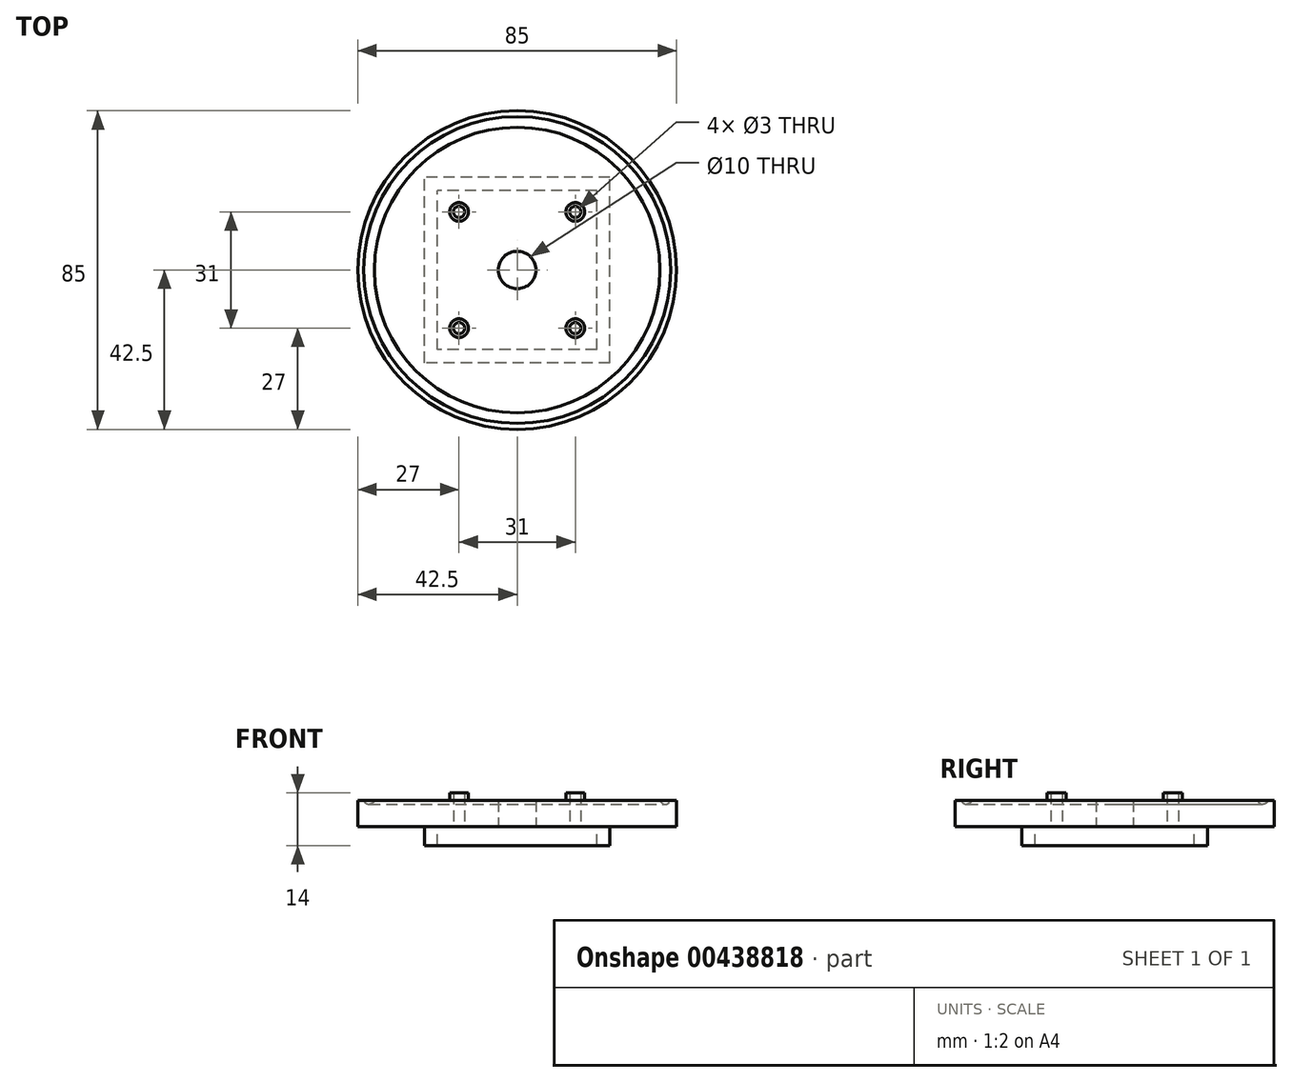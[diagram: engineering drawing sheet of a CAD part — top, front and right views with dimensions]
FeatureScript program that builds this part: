
annotation { "Feature Type Name" : "Feature", "Feature Type Description" : "" }
export const myFeature = defineFeature(function(context is Context, id is Id, definition is map)
    precondition{}
    {
        {
            var Q0;
            Q0=qCreatedBy(makeId("Top.planeOp"),FACE);
            var sketch = newSketch(context, id + "F0", { "sketchPlane" : qUnion([Q0])});
            skCircle(sketch, "E0", {"center": v(0, 0) * mm, "radius": 42.5 * mm});
            skLineSegment(sketch, "E1.bottom", {"start": v(21.25, 21.25) * mm, "end": v(-21.25, 21.25) * mm, "construction": true});
            skLineSegment(sketch, "E1.top", {"start": v(21.25, -21.25) * mm, "end": v(-21.25, -21.25) * mm, "construction": true});
            skLineSegment(sketch, "E1.left", {"start": v(21.25, 21.25) * mm, "end": v(21.25, -21.25) * mm, "construction": true});
            skLineSegment(sketch, "E1.right", {"start": v(-21.25, 21.25) * mm, "end": v(-21.25, -21.25) * mm, "construction": true});
            skLineSegment(sketch, "E2.bottom", {"start": v(15.5, 15.5) * mm, "end": v(-15.5, 15.5) * mm, "construction": true});
            skLineSegment(sketch, "E2.top", {"start": v(15.5, -15.5) * mm, "end": v(-15.5, -15.5) * mm, "construction": true});
            skLineSegment(sketch, "E2.left", {"start": v(15.5, 15.5) * mm, "end": v(15.5, -15.5) * mm, "construction": true});
            skLineSegment(sketch, "E2.right", {"start": v(-15.5, 15.5) * mm, "end": v(-15.5, -15.5) * mm, "construction": true});
            skCircle(sketch, "E3", {"center": v(-15.5, 15.5) * mm, "radius": 1.5 * mm});
            skCircle(sketch, "E4", {"center": v(15.5, 15.5) * mm, "radius": 1.5 * mm});
            skCircle(sketch, "E5", {"center": v(15.5, -15.5) * mm, "radius": 1.5 * mm});
            skCircle(sketch, "E6", {"center": v(-15.5, -15.5) * mm, "radius": 1.5 * mm});
            skCircle(sketch, "E7", {"center": v(0, 0) * mm, "radius": 5 * mm});
            skSolve(sketch);
        }
        {
            var Q0;
            Q0=makeQuery(id+"F0.imprint","IMPRINT",FACE,{"disambiguationData":[TD([[makeQuery(id+"F0.imprint","IMPRINT",EDGE,{"derivedFrom":sQuery(id+"F0.wireOp",EDGE,"E0")}),1.0]])]});
            extrude(context, id + "F1", {"entities" : qUnion([Q0]), "depth" : 7 * mm});
        }
        {
            var Q0;
            Q0=makeQuery(id+"F1.opExtrude","CAP_FACE",FACE,{"disambiguationData":[OSD([sQuery(id+"F0.wireOp",EDGE,"E0"),sQuery(id+"F0.wireOp",EDGE,"E3"),sQuery(id+"F0.wireOp",EDGE,"E4"),sQuery(id+"F0.wireOp",EDGE,"E5"),sQuery(id+"F0.wireOp",EDGE,"E6")])],"isStart":false});
            cPlane(context, id + "F2", {"entities" : qUnion([Q0]), "cplaneType" : CPlaneType.OFFSET, "offset" : 0 * mm, "width" : 150 * mm, "height" : 150 * mm});
        }
        {
            var Q0;
            Q0=makeQuery(id+"F1.opExtrude","CAP_FACE",FACE,{"disambiguationData":[OSD([sQuery(id+"F0.wireOp",EDGE,"E0"),sQuery(id+"F0.wireOp",EDGE,"E3"),sQuery(id+"F0.wireOp",EDGE,"E4"),sQuery(id+"F0.wireOp",EDGE,"E5"),sQuery(id+"F0.wireOp",EDGE,"E6"),sQuery(id+"F0.wireOp",EDGE,"E7")])],"isStart":true});
            var sketch = newSketch(context, id + "F3", { "sketchPlane" : qUnion([Q0])});
            skLineSegment(sketch, "E8.bottom", {"start": v(21.25, 21.25) * mm, "end": v(-21.25, 21.25) * mm});
            skLineSegment(sketch, "E8.top", {"start": v(21.25, -21.25) * mm, "end": v(-21.25, -21.25) * mm});
            skLineSegment(sketch, "E8.left", {"start": v(21.25, 21.25) * mm, "end": v(21.25, -21.25) * mm});
            skLineSegment(sketch, "E8.right", {"start": v(-21.25, 21.25) * mm, "end": v(-21.25, -21.25) * mm});
            skPoint(sketch, "E8.middle", {"position": v(0, 0) * mm});
            skLineSegment(sketch, "E9.bottom", {"start": v(24.75, 24.75) * mm, "end": v(-24.75, 24.75) * mm});
            skLineSegment(sketch, "E9.top", {"start": v(24.75, -24.75) * mm, "end": v(-24.75, -24.75) * mm});
            skLineSegment(sketch, "E9.left", {"start": v(24.75, 24.75) * mm, "end": v(24.75, -24.75) * mm});
            skLineSegment(sketch, "E9.right", {"start": v(-24.75, 24.75) * mm, "end": v(-24.75, -24.75) * mm});
            skSolve(sketch);
        }
        {
            var Q0;
            Q0=makeQuery(id+"F3.imprint","IMPRINT",FACE,{"disambiguationData":[TD([[makeQuery(id+"F3.imprint","IMPRINT",EDGE,{"derivedFrom":sQuery(id+"F3.wireOp",EDGE,"E8.bottom")}),-1.0]])]});
            extrude(context, id + "F4", {"entities" : qUnion([Q0]), "operationType" : NewBodyOperationType.ADD, "depth" : 5 * mm});
        }
        {
            var Q0;
            Q0=qCreatedBy(id+"F2.planeOp",FACE);
            var sketch = newSketch(context, id + "F5", { "sketchPlane" : qUnion([Q0])});
            skCircle(sketch, "E10.0", {"center": v(-15.5, 15.5) * mm, "radius": 1.5 * mm});
            skCircle(sketch, "E11.0", {"center": v(15.5, 15.5) * mm, "radius": 1.5 * mm});
            skCircle(sketch, "E12.0", {"center": v(15.5, -15.5) * mm, "radius": 1.5 * mm});
            skCircle(sketch, "E13.0", {"center": v(-15.5, -15.5) * mm, "radius": 1.5 * mm});
            skCircle(sketch, "E14", {"center": v(-15.5, 15.5) * mm, "radius": 2.5 * mm});
            skCircle(sketch, "E15", {"center": v(15.5, 15.5) * mm, "radius": 2.5 * mm});
            skCircle(sketch, "E16", {"center": v(15.5, -15.5) * mm, "radius": 2.5 * mm});
            skCircle(sketch, "E17", {"center": v(-15.5, -15.5) * mm, "radius": 2.5 * mm});
            skSolve(sketch);
        }
        {
            var Q0;
            Q0 = qSketchRegion(id + "F5", true);
            extrude(context, id + "F6", {"entities" : qUnion([Q0]), "operationType" : NewBodyOperationType.ADD, "depth" : 2 * mm});
        }
        {
            var Q0;
            Q0=qCreatedBy(makeId("Right.planeOp"),FACE);
            var sketch = newSketch(context, id + "F7", { "sketchPlane" : qUnion([Q0])});
            skCircle(sketch, "E18", {"center": v(-39.5, 7.5) * mm, "radius": 1.5 * mm});
            skLineSegment(sketch, "E19", {"start": v(-42.5, 0) * mm, "end": v(-42.5, 7) * mm});
            skLineSegment(sketch, "E20", {"start": v(-42.5, 0) * mm, "end": v(-42.5, 7) * mm, "construction": true});
            skSolve(sketch);
        }
        {
            var Q0;
            Q0=makeQuery(id+"F7.imprint","IMPRINT",FACE,{"disambiguationData":[TD([[makeQuery(id+"F7.imprint","IMPRINT",EDGE,{"derivedFrom":sQuery(id+"F7.wireOp",EDGE,"E18")}),1.0]])]});
            var Q1;
            Q1=makeQuery(id+"F1.opExtrude","CAP_EDGE",EDGE,{"disambiguationData":[OSD([sQuery(id+"F0.wireOp",EDGE,"E7")])],"isStart":false});
            revolve(context, id + "F8", {"operationType" : NewBodyOperationType.REMOVE, "entities" : qUnion([Q0]), "axis" : qUnion([Q1]), "revolveType" : RevolveType.FULL, "oppositeDirection" : true});
        }
    });
